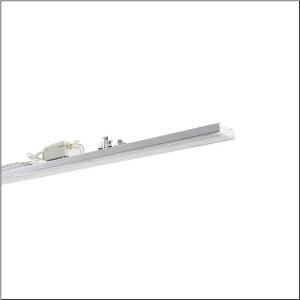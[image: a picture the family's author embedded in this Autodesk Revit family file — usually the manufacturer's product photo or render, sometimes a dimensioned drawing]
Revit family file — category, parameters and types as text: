
# Revit family: licross_r__21_recessed_mo_52tl12dn4axg_5465
name_source: partatom
category: Lighting Fixtures
units: mm (PartAtom-declared; Revit-internal decimal feet)

## family parameters
Cut with Voids When Loaded = No
Host = Face
Light Source = No
Part Type = Normal
Room Calculation Point = No
Round Connector Dimension = Use Diameter
Shared = No

## types (1)
- --- (1 x LED, 10280 lm, 58 W, 4000K)
    Apparent Load = 58 VA
    CIE Flux Codes = 72 92 99 100 100
    Color Rendering = 80
    Color Temperature = 4000K
    Default Elevation = 1800 mm
    Description = Licross® 21 Recessed MO, luminaire insert, of sheet steel, galvanised, coil coated, white, length: 1.500mm, width: 66mm, height: 67mm, LED rated luminous flux: 10.280lm, light colour: 840, control gear: DALI 2, with plug, 5-pole, with phase selection, mains connection: 220..240V, AC, 50/60Hz, rated input power: 58W, halogen-free wiring, primary optical cover: cover, of PMMA, light emission: direct distribution, primary light characteristic: symmetric, protection rating (complete): IP40, insulation class (complete): insulation class I (protective earthing), certification: CE, ENEC, VDE, UKCA, protection symbol: D if used in an environment without relevant dust loads with corresponding accessories, impact resistance: IK06, permissible ambient temperature for indoor applications: -25..+35°C, corresponds to IFS (International Featured Standards) requirements for safety and quality in the food industry, reducing of maximum allowable ambient temperature of 5°C with ceiling mounting, LABS conformity tested according to VDMA 24364:2018-05, packaging unit: 1 piece
    Height = 58 mm
    Lamp = 1 x LED
    Lamp Light Flux = 10280 lm
    Lamp Power = 58 W
    Lamp count = 1
    Length = 1500 mm
    Luminous efficacy = 177 lm/W
    Manufacturer = Siteco
    ModVariant = No
    Model = 52TL12DN4AXG
    Mounting Place = Ceiling
    Mounting Type = Pendant
    Number of Poles = 1
    OnlyDefault = Yes
    Power Factor = 1
    Product Name = Licross® 21 Recessed MO
    Product group = luminaire insert
    ProductGroupID = 901
    Protection Class = Protection class I
    Protection Degree = IP 40
    RLX_Detail_Level = 1
    RLX_Emergency_Light_Flux = 0 lm
    RLX_Emergency_Type = 0
    RLX_Emergency_Type_DB = No
    RlxData = <blob elided: 24585 chars, md5=40b85857>
    Socket = socket
    Standby Power = 0 W
    System Light Flux = 10280 lm
    System Power = 58 W
    Type Comments = factory setting: luminous flux: 100 % | dim-lin: 254 | 390 mA
    Type Image = l_1296930.jpg
    URL = http://relux.com
    VarID = @adj_057863
    Voltage = 0 V
    Weight = 0.00 kg
    Width = 66 mm

## geometry (parser evidence)
native form markers: Blend x4, Sweep x12
no freeform markers — native parametric forms only
